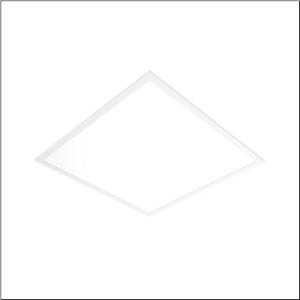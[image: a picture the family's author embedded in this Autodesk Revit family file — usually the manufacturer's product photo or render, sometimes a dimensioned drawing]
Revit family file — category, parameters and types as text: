
# Revit family: apollon_r__41_51mh12w72443m_8ad7
name_source: partatom
category: Lighting Fixtures
units: mm (PartAtom-declared; Revit-internal decimal feet)

## family parameters
Cut with Voids When Loaded = No
Host = Face
Light Source = No
Part Type = Normal
Room Calculation Point = No
Round Connector Dimension = Use Diameter
Shared = No

## types (1)
- Apollon® 41 (1 x LED, 3700 lm, 28.5 W, 4000K)
    Apparent Load = 29 VA
    CIE Flux Codes = 61 87 97 100 100
    Color Rendering = 80
    Color Temperature = 4000K
    Default Elevation = 1800 mm
    Description = Apollon® 41, office luminaire, primary optical cover: prismatic diffuser, of PS, light emission: direct distribution, primary light characteristic: symmetric, installation type: lay-in mounting, LED, rated luminous flux: 3.700lm, luminous efficacy: 130lm/W, light colour: 840, colour temperature: 4000K, with terminal, 3-pole, mains connection: 220..240V, AC, 50/60Hz, housing, of aluminium section, traffic white (RAL 9016), module: M600, length: 600mm, width: 600mm, height: 28mm, housing upper side, of sheet steel, protection rating (complete): IP20, protection rating (lamp compartment, on room side): IP40, insulation class (complete): insulation class II (safety insulation), certification: CE, ENEC, permissible operating ambient temperature: -25..+40°C, packaging unit: set of 6
    Height = 0 mm  [stored 0 ft]
    Lamp = 1 x LED
    Lamp Light Flux = 3700 lm
    Lamp Power = 28.5 W
    Lamp count = 1
    Length = 600 mm
    Luminous efficacy = 130 lm/W
    Manufacturer = Siteco
    ModVariant = No
    Model = 51MH12W72443M
    Mounting Place = Ceiling
    Mounting Type = Recessed
    Number of Poles = 1
    OnlyDefault = Yes
    Power Factor = 1
    Product Name = Apollon® 41
    Product group = office luminaire | ceiling recessed
    ProductGroupID = 401
    Protection Class = Protection class II
    Protection Degree = IP 20
    RLX_Detail_Level = 1
    RLX_Emergency_Light_Flux = 0 lm
    RLX_Emergency_Type = 0
    RLX_Emergency_Type_DB = No
    RlxData = <blob elided: 12201 chars, md5=3e7c49ed>
    Socket = socket
    Standby Power = 0 W
    System Light Flux = 3700 lm
    System Power = 29 W
    Type Comments = Product without accessories
    Type Image = l_1291024.jpg
    URL = http://relux.com
    VarID = ---
    Voltage = 0 V
    Weight = 0.00 kg
    Width = 600 mm

note: [stored X ft] marks values corroborated as IEEE doubles in the binary element streams (Revit-internal decimal feet)

## geometry (parser evidence)
native form markers: Sweep x11
no freeform markers — native parametric forms only
